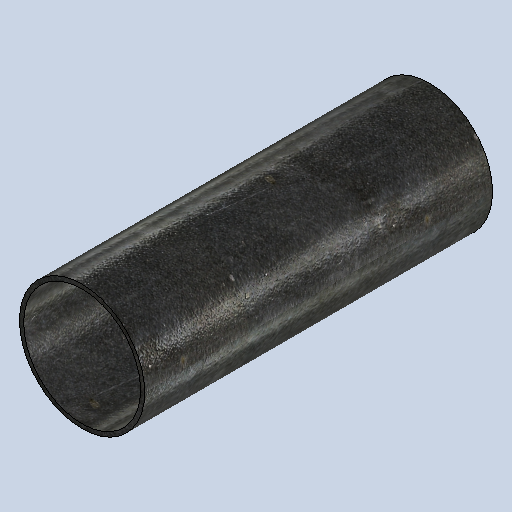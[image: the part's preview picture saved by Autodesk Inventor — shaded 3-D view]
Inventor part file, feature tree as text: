
AUTODESK INVENTOR PART (.ipt)
format: ipt  version: 2025.1 (Build 291241020, 241B)  size: 266,752 bytes
history: native  units: mm
features: extrude x1, sketch x1
ambient origin geometry x8: Origin, YZ Plane, XZ Plane, XY Plane, X Axis, Y Axis, Z Axis, Center Point
bodies: Solid1 (feature_tree)
feature tree (2):
  extrude  "Extrusion1"  Depth=250.0mm
  sketch  "Sketch1"  dims[d0=90.0mm d1=3.0mm d2=250.0mm d3=0.0mm]
